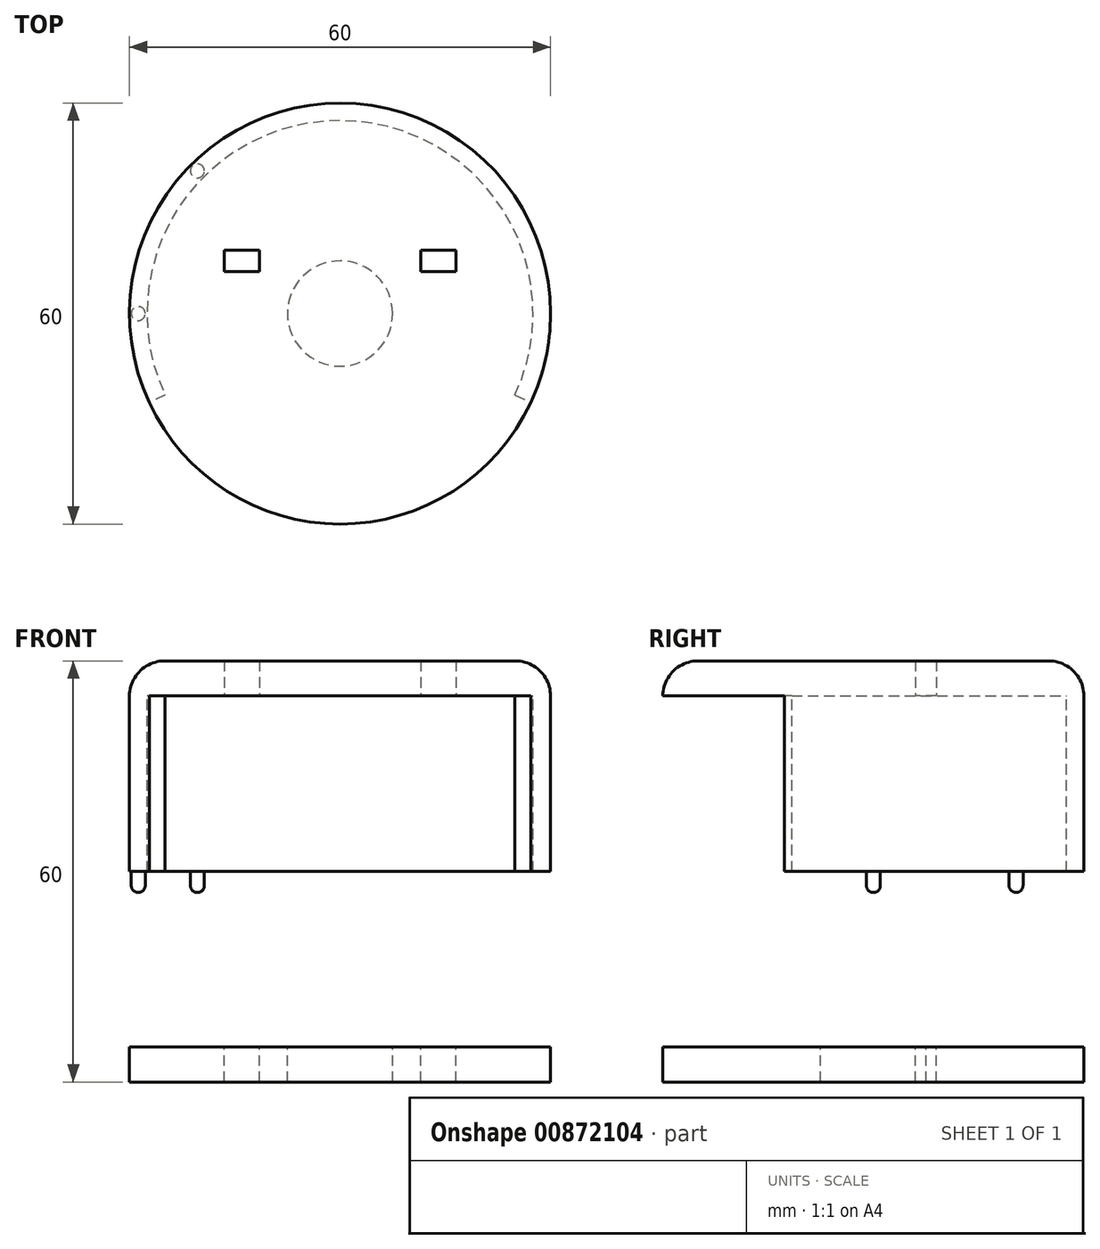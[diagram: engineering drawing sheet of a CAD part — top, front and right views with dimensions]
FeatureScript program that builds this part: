
annotation { "Feature Type Name" : "Feature", "Feature Type Description" : "" }
export const myFeature = defineFeature(function(context is Context, id is Id, definition is map)
    precondition{}
    {
        {
            var Q0;
            Q0=qCreatedBy(makeId("Top.planeOp"),FACE);
            var sketch = newSketch(context, id + "F0", { "sketchPlane" : qUnion([Q0])});
            skCircle(sketch, "E0", {"center": v(0, 0) * mm, "radius": 30 * mm});
            skLineSegment(sketch, "E1", {"start": v(0, 0) * mm, "end": v(0, 7.5) * mm});
            skLineSegment(sketch, "E2", {"start": v(0, 7.5) * mm, "end": v(14, 7.5) * mm});
            skLineSegment(sketch, "E3.bottom", {"start": v(11.5, 9) * mm, "end": v(16.5, 9) * mm});
            skLineSegment(sketch, "E3.top", {"start": v(11.5, 6) * mm, "end": v(16.5, 6) * mm});
            skLineSegment(sketch, "E3.left", {"start": v(11.5, 9) * mm, "end": v(11.5, 6) * mm});
            skLineSegment(sketch, "E3.right", {"start": v(16.5, 9) * mm, "end": v(16.5, 6) * mm});
            skPoint(sketch, "E3.middle", {"position": v(14, 7.5) * mm});
            skLineSegment(sketch, "E4", {"start": v(0, 7.5) * mm, "end": v(-14, 7.5) * mm});
            skLineSegment(sketch, "E5.bottom", {"start": v(-16.5, 9) * mm, "end": v(-11.5, 9) * mm});
            skLineSegment(sketch, "E5.top", {"start": v(-16.5, 6) * mm, "end": v(-11.5, 6) * mm});
            skLineSegment(sketch, "E5.left", {"start": v(-16.5, 9) * mm, "end": v(-16.5, 6) * mm});
            skLineSegment(sketch, "E5.right", {"start": v(-11.5, 9) * mm, "end": v(-11.5, 6) * mm});
            skPoint(sketch, "E5.middle", {"position": v(-14, 7.5) * mm});
            skLineSegment(sketch, "E6", {"start": v(0, 0) * mm, "end": v(-27.19, -12.68) * mm});
            skLineSegment(sketch, "E7", {"start": v(0, 0) * mm, "end": v(27.19, -12.68) * mm});
            skCircle(sketch, "E8", {"center": v(0, 0) * mm, "radius": 27.5 * mm});
            skCircle(sketch, "E9", {"center": v(0, 0) * mm, "radius": 7.5 * mm});
            skSolve(sketch);
        }
        {
            var Q0;
            Q0=makeQuery(id+"F0.imprint","IMPRINT",FACE,{"disambiguationData":[TD([[makeQuery(id+"F0.imprint","IMPRINT",EDGE,{"derivedFrom":sQuery(id+"F0.wireOp",EDGE,"E0")}),1.0]])]});
            var Q1;
            {var subQ4=sQuery(id+"F0.wireOp",EDGE,"E3.bottom");Q1=makeQuery(id+"F0.imprint","IMPRINT",FACE,{"disambiguationData":[TD([[makeQuery(id+"F0.imprint","IMPRINT",EDGE,{"derivedFrom":subQ4}),1.0]])]});}
            var Q2;
            {var subQ0=sQuery(id+"F0.wireOp",EDGE,"E9");var subQ1=sQuery(id+"F0.wireOp",EDGE,"E6");var subQ2=makeQuery(id+"F0.imprint","INTERSECT",VERTEX,{"derivedFrom":[subQ1,subQ0]});Q2=makeQuery(id+"F0.imprint","IMPRINT",FACE,{"disambiguationData":[TD([[makeQuery(id+"F0.imprint","IMPRINT",EDGE,{"disambiguationData":[TD([[subQ2,-1.0]])],"derivedFrom":subQ1}),1.0]])]});}
            extrude(context, id + "F1", {"entities" : qUnion([Q0, Q1, Q2]), "oppositeDirection" : true, "depth" : 5 * mm, "offsetDistance" : 25 * mm});
        }
        {
            var Q0;
            Q0=makeQuery(id+"F1.opExtrude","CAP_FACE",FACE,{"disambiguationData":[OSD([sQuery(id+"F0.wireOp",EDGE,"E0")])],"isStart":true});
            cPlane(context, id + "F2", {"entities" : qUnion([Q0]), "cplaneType" : CPlaneType.OFFSET, "offset" : 50 * mm, "width" : 150 * mm, "height" : 150 * mm});
        }
        {
            var Q0;
            Q0=qCreatedBy(id+"F2.planeOp",FACE);
            var sketch = newSketch(context, id + "F3", { "sketchPlane" : qUnion([Q0])});
            skCircle(sketch, "E10", {"center": v(0, 0) * mm, "radius": 30 * mm});
            skLineSegment(sketch, "E11", {"start": v(0, 0) * mm, "end": v(0, 7.5) * mm});
            skLineSegment(sketch, "E12", {"start": v(0, 7.5) * mm, "end": v(14, 7.5) * mm});
            skLineSegment(sketch, "E13", {"start": v(0, 7.5) * mm, "end": v(-14, 7.5) * mm});
            skLineSegment(sketch, "E14.bottom", {"start": v(-16.5, 9) * mm, "end": v(-11.5, 9) * mm});
            skLineSegment(sketch, "E14.top", {"start": v(-16.5, 6) * mm, "end": v(-11.5, 6) * mm});
            skLineSegment(sketch, "E14.left", {"start": v(-16.5, 9) * mm, "end": v(-16.5, 6) * mm});
            skLineSegment(sketch, "E14.right", {"start": v(-11.5, 9) * mm, "end": v(-11.5, 6) * mm});
            skPoint(sketch, "E14.middle", {"position": v(-14, 7.5) * mm});
            skLineSegment(sketch, "E15.bottom", {"start": v(16.5, 9) * mm, "end": v(11.5, 9) * mm});
            skLineSegment(sketch, "E15.top", {"start": v(16.5, 6) * mm, "end": v(11.5, 6) * mm});
            skLineSegment(sketch, "E15.left", {"start": v(16.5, 9) * mm, "end": v(16.5, 6) * mm});
            skLineSegment(sketch, "E15.right", {"start": v(11.5, 9) * mm, "end": v(11.5, 6) * mm});
            skPoint(sketch, "E15.middle", {"position": v(14, 7.5) * mm});
            skLineSegment(sketch, "E16", {"start": v(0, 0) * mm, "end": v(30, 0) * mm});
            skLineSegment(sketch, "E17", {"start": v(0, 0) * mm, "end": v(-30, 0) * mm});
            skCircle(sketch, "E18", {"center": v(0, 0) * mm, "radius": 27.5 * mm});
            skLineSegment(sketch, "E19", {"start": v(0, 0) * mm, "end": v(-27.19, -12.68) * mm});
            skLineSegment(sketch, "E20", {"start": v(0, 0) * mm, "end": v(27.19, -12.68) * mm});
            skLineSegment(sketch, "E21", {"start": v(0, 0) * mm, "end": v(-21.21, 21.21) * mm});
            skLineSegment(sketch, "E22", {"start": v(0, 0) * mm, "end": v(21.21, 21.21) * mm});
            skCircle(sketch, "E23", {"center": v(-28.75, 0) * mm, "radius": 1 * mm});
            skCircle(sketch, "E24", {"center": v(-20.33, 20.33) * mm, "radius": 1 * mm});
            skSolve(sketch);
        }
        {
            var Q0;
            {var subQ7=sQuery(id+"F3.wireOp",EDGE,"E14.bottom");Q0=makeQuery(id+"F3.imprint","IMPRINT",FACE,{"disambiguationData":[TD([[makeQuery(id+"F3.imprint","IMPRINT",EDGE,{"derivedFrom":subQ7}),1.0]])]});}
            var Q1;
            {var subQ1=sQuery(id+"F3.wireOp",EDGE,"E17");var subQ3=sQuery(id+"F3.wireOp",EDGE,"E18");var subQ4=makeQuery(id+"F3.imprint","INTERSECT",VERTEX,{"derivedFrom":[subQ1,subQ3]});Q1=makeQuery(id+"F3.imprint","IMPRINT",FACE,{"disambiguationData":[TD([[makeQuery(id+"F3.imprint","IMPRINT",EDGE,{"disambiguationData":[TD([[subQ4,-1.0]])],"derivedFrom":subQ3}),1.0]])]});}
            var Q2;
            {var subQ0=sQuery(id+"F3.wireOp",EDGE,"E19");var subQ1=sQuery(id+"F3.wireOp",EDGE,"E18");var subQ2=makeQuery(id+"F3.imprint","INTERSECT",VERTEX,{"derivedFrom":[subQ1,subQ0]});Q2=makeQuery(id+"F3.imprint","IMPRINT",FACE,{"disambiguationData":[TD([[makeQuery(id+"F3.imprint","IMPRINT",EDGE,{"disambiguationData":[TD([[subQ2,-1.0]])],"derivedFrom":subQ1}),1.0]])]});}
            var Q3;
            {var subQ1=sQuery(id+"F3.wireOp",EDGE,"E16");var subQ3=sQuery(id+"F3.wireOp",EDGE,"E18");var subQ4=makeQuery(id+"F3.imprint","INTERSECT",VERTEX,{"derivedFrom":[subQ1,subQ3]});Q3=makeQuery(id+"F3.imprint","IMPRINT",FACE,{"disambiguationData":[TD([[makeQuery(id+"F3.imprint","IMPRINT",EDGE,{"disambiguationData":[TD([[subQ4,1.0]])],"derivedFrom":subQ3}),1.0]])]});}
            var Q4;
            {var subQ0=sQuery(id+"F3.wireOp",EDGE,"E17");var subQ1=sQuery(id+"F3.wireOp",EDGE,"E10");var subQ2=makeQuery(id+"F3.imprint","INTERSECT",VERTEX,{"derivedFrom":[subQ1,subQ0]});Q4=makeQuery(id+"F3.imprint","IMPRINT",FACE,{"disambiguationData":[TD([[makeQuery(id+"F3.imprint","IMPRINT",EDGE,{"disambiguationData":[TD([[subQ2,-1.0]])],"derivedFrom":subQ1}),1.0]])]});}
            var Q5;
            {var subQ0=sQuery(id+"F3.wireOp",EDGE,"E19");var subQ1=sQuery(id+"F3.wireOp",EDGE,"E10");var subQ2=makeQuery(id+"F3.imprint","INTERSECT",VERTEX,{"derivedFrom":[subQ1,subQ0]});Q5=makeQuery(id+"F3.imprint","IMPRINT",FACE,{"disambiguationData":[TD([[makeQuery(id+"F3.imprint","IMPRINT",EDGE,{"disambiguationData":[TD([[subQ2,-1.0]])],"derivedFrom":subQ1}),1.0]])]});}
            var Q6;
            {var subQ0=sQuery(id+"F3.wireOp",EDGE,"E16");var subQ1=sQuery(id+"F3.wireOp",EDGE,"E10");var subQ2=makeQuery(id+"F3.imprint","INTERSECT",VERTEX,{"derivedFrom":[subQ1,subQ0]});Q6=makeQuery(id+"F3.imprint","IMPRINT",FACE,{"disambiguationData":[TD([[makeQuery(id+"F3.imprint","IMPRINT",EDGE,{"disambiguationData":[TD([[subQ2,1.0]])],"derivedFrom":subQ1}),1.0]])]});}
            var Q7;
            {var subQ0=sQuery(id+"F3.wireOp",EDGE,"E16");var subQ1=sQuery(id+"F3.wireOp",EDGE,"E10");var subQ2=makeQuery(id+"F3.imprint","INTERSECT",VERTEX,{"derivedFrom":[subQ1,subQ0]});Q7=makeQuery(id+"F3.imprint","IMPRINT",FACE,{"disambiguationData":[TD([[makeQuery(id+"F3.imprint","IMPRINT",EDGE,{"disambiguationData":[TD([[subQ2,-1.0]])],"derivedFrom":subQ1}),1.0]])]});}
            var Q8;
            {var subQ1=sQuery(id+"F3.wireOp",EDGE,"E15.bottom");Q8=makeQuery(id+"F3.imprint","IMPRINT",FACE,{"disambiguationData":[TD([[makeQuery(id+"F3.imprint","IMPRINT",EDGE,{"derivedFrom":subQ1}),-1.0]])]});}
            var Q9;
            {var subQ0=sQuery(id+"F3.wireOp",EDGE,"E23");var subQ1=sQuery(id+"F3.wireOp",EDGE,"E17");var subQ2=makeQuery(id+"F3.imprint","INTERSECT",VERTEX,{"disambiguationData":[OD(0.0)],"derivedFrom":[subQ1,subQ0]});Q9=makeQuery(id+"F3.imprint","IMPRINT",FACE,{"disambiguationData":[TD([[makeQuery(id+"F3.imprint","IMPRINT",EDGE,{"disambiguationData":[TD([[subQ2,-1.0]])],"derivedFrom":subQ1}),-1.0]])]});}
            var Q10;
            {var subQ0=sQuery(id+"F3.wireOp",EDGE,"E23");var subQ1=sQuery(id+"F3.wireOp",EDGE,"E17");var subQ2=makeQuery(id+"F3.imprint","INTERSECT",VERTEX,{"disambiguationData":[OD(0.0)],"derivedFrom":[subQ1,subQ0]});Q10=makeQuery(id+"F3.imprint","IMPRINT",FACE,{"disambiguationData":[TD([[makeQuery(id+"F3.imprint","IMPRINT",EDGE,{"disambiguationData":[TD([[subQ2,-1.0]])],"derivedFrom":subQ1}),1.0]])]});}
            var Q11;
            {var subQ0=sQuery(id+"F3.wireOp",EDGE,"E17");var subQ1=sQuery(id+"F3.wireOp",EDGE,"E10");var subQ2=makeQuery(id+"F3.imprint","INTERSECT",VERTEX,{"derivedFrom":[subQ1,subQ0]});Q11=makeQuery(id+"F3.imprint","IMPRINT",FACE,{"disambiguationData":[TD([[makeQuery(id+"F3.imprint","IMPRINT",EDGE,{"disambiguationData":[TD([[subQ2,1.0]])],"derivedFrom":subQ1}),1.0]])]});}
            var Q12;
            {var subQ0=sQuery(id+"F3.wireOp",EDGE,"E24");var subQ1=sQuery(id+"F3.wireOp",EDGE,"E21");var subQ2=makeQuery(id+"F3.imprint","INTERSECT",VERTEX,{"disambiguationData":[OD(0.0)],"derivedFrom":[subQ1,subQ0]});Q12=makeQuery(id+"F3.imprint","IMPRINT",FACE,{"disambiguationData":[TD([[makeQuery(id+"F3.imprint","IMPRINT",EDGE,{"disambiguationData":[TD([[subQ2,-1.0]])],"derivedFrom":subQ1}),1.0]])]});}
            var Q13;
            {var subQ0=sQuery(id+"F3.wireOp",EDGE,"E24");var subQ1=sQuery(id+"F3.wireOp",EDGE,"E21");var subQ2=makeQuery(id+"F3.imprint","INTERSECT",VERTEX,{"disambiguationData":[OD(0.0)],"derivedFrom":[subQ1,subQ0]});Q13=makeQuery(id+"F3.imprint","IMPRINT",FACE,{"disambiguationData":[TD([[makeQuery(id+"F3.imprint","IMPRINT",EDGE,{"disambiguationData":[TD([[subQ2,-1.0]])],"derivedFrom":subQ1}),-1.0]])]});}
            var Q14;
            {var subQ0=sQuery(id+"F3.wireOp",EDGE,"E21");var subQ1=sQuery(id+"F3.wireOp",EDGE,"E10");var subQ2=makeQuery(id+"F3.imprint","INTERSECT",VERTEX,{"derivedFrom":[subQ1,subQ0]});Q14=makeQuery(id+"F3.imprint","IMPRINT",FACE,{"disambiguationData":[TD([[makeQuery(id+"F3.imprint","IMPRINT",EDGE,{"disambiguationData":[TD([[subQ2,1.0]])],"derivedFrom":subQ1}),1.0]])]});}
            var Q15;
            {var subQ3=sQuery(id+"F3.wireOp",EDGE,"E18");var subQ5=sQuery(id+"F3.wireOp",EDGE,"E22");var subQ6=makeQuery(id+"F3.imprint","INTERSECT",VERTEX,{"derivedFrom":[subQ3,subQ5]});Q15=makeQuery(id+"F3.imprint","IMPRINT",FACE,{"disambiguationData":[TD([[makeQuery(id+"F3.imprint","IMPRINT",EDGE,{"disambiguationData":[TD([[subQ6,-1.0]])],"derivedFrom":subQ3}),1.0]])]});}
            var Q16;
            {var subQ0=sQuery(id+"F3.wireOp",EDGE,"E11");Q16=makeQuery(id+"F3.imprint","IMPRINT",FACE,{"disambiguationData":[TD([[makeQuery(id+"F3.imprint","IMPRINT",EDGE,{"derivedFrom":subQ0}),1.0]])]});}
            var Q17;
            {var subQ0=sQuery(id+"F3.wireOp",EDGE,"E11");Q17=makeQuery(id+"F3.imprint","IMPRINT",FACE,{"disambiguationData":[TD([[makeQuery(id+"F3.imprint","IMPRINT",EDGE,{"derivedFrom":subQ0}),-1.0]])]});}
            extrude(context, id + "F4", {"entities" : qUnion([Q0, Q1, Q2, Q3, Q4, Q5, Q6, Q7, Q8, Q9, Q10, Q11, Q12, Q13, Q14, Q15, Q16, Q17]), "depth" : 5 * mm, "offsetDistance" : 25 * mm});
        }
        {
            var Q0;
            Q0=makeQuery(id+"F4.opExtrude","CAP_EDGE",EDGE,{"disambiguationData":[OSD([sQuery(id+"F3.wireOp",EDGE,"E10")])],"isStart":false});
            fillet(context, id + "F5", {"entities" : qUnion([Q0]), "radius" : 5 * mm, "tangentPropagation" : true, "allowEdgeOverflow" : false});
        }
        {
            var Q0;
            {var subQ0=sQuery(id+"F3.wireOp",EDGE,"E17");var subQ1=sQuery(id+"F3.wireOp",EDGE,"E10");var subQ2=makeQuery(id+"F3.imprint","INTERSECT",VERTEX,{"derivedFrom":[subQ1,subQ0]});Q0=makeQuery(id+"F3.imprint","IMPRINT",FACE,{"disambiguationData":[TD([[makeQuery(id+"F3.imprint","IMPRINT",EDGE,{"disambiguationData":[TD([[subQ2,-1.0]])],"derivedFrom":subQ1}),1.0]])]});}
            var Q1;
            {var subQ0=sQuery(id+"F3.wireOp",EDGE,"E16");var subQ1=sQuery(id+"F3.wireOp",EDGE,"E10");var subQ2=makeQuery(id+"F3.imprint","INTERSECT",VERTEX,{"derivedFrom":[subQ1,subQ0]});Q1=makeQuery(id+"F3.imprint","IMPRINT",FACE,{"disambiguationData":[TD([[makeQuery(id+"F3.imprint","IMPRINT",EDGE,{"disambiguationData":[TD([[subQ2,-1.0]])],"derivedFrom":subQ1}),1.0]])]});}
            var Q2;
            {var subQ0=sQuery(id+"F3.wireOp",EDGE,"E16");var subQ1=sQuery(id+"F3.wireOp",EDGE,"E10");var subQ2=makeQuery(id+"F3.imprint","INTERSECT",VERTEX,{"derivedFrom":[subQ1,subQ0]});Q2=makeQuery(id+"F3.imprint","IMPRINT",FACE,{"disambiguationData":[TD([[makeQuery(id+"F3.imprint","IMPRINT",EDGE,{"disambiguationData":[TD([[subQ2,1.0]])],"derivedFrom":subQ1}),1.0]])]});}
            var Q3;
            {var subQ0=sQuery(id+"F3.wireOp",EDGE,"E17");var subQ1=sQuery(id+"F3.wireOp",EDGE,"E10");var subQ2=makeQuery(id+"F3.imprint","INTERSECT",VERTEX,{"derivedFrom":[subQ1,subQ0]});Q3=makeQuery(id+"F3.imprint","IMPRINT",FACE,{"disambiguationData":[TD([[makeQuery(id+"F3.imprint","IMPRINT",EDGE,{"disambiguationData":[TD([[subQ2,1.0]])],"derivedFrom":subQ1}),1.0]])]});}
            var Q4;
            {var subQ0=sQuery(id+"F3.wireOp",EDGE,"E21");var subQ1=sQuery(id+"F3.wireOp",EDGE,"E10");var subQ2=makeQuery(id+"F3.imprint","INTERSECT",VERTEX,{"derivedFrom":[subQ1,subQ0]});Q4=makeQuery(id+"F3.imprint","IMPRINT",FACE,{"disambiguationData":[TD([[makeQuery(id+"F3.imprint","IMPRINT",EDGE,{"disambiguationData":[TD([[subQ2,1.0]])],"derivedFrom":subQ1}),1.0]])]});}
            extrude(context, id + "F6", {"entities" : qUnion([Q0, Q1, Q2, Q3, Q4]), "operationType" : NewBodyOperationType.ADD, "oppositeDirection" : true, "depth" : 25 * mm, "offsetDistance" : 25 * mm});
        }
        {
            var Q0;
            {var subQ0=sQuery(id+"F3.wireOp",EDGE,"E23");var subQ1=sQuery(id+"F3.wireOp",EDGE,"E17");var subQ2=makeQuery(id+"F3.imprint","INTERSECT",VERTEX,{"disambiguationData":[OD(0.0)],"derivedFrom":[subQ1,subQ0]});Q0=makeQuery(id+"F3.imprint","IMPRINT",FACE,{"disambiguationData":[TD([[makeQuery(id+"F3.imprint","IMPRINT",EDGE,{"disambiguationData":[TD([[subQ2,-1.0]])],"derivedFrom":subQ1}),1.0]])]});}
            var Q1;
            {var subQ0=sQuery(id+"F3.wireOp",EDGE,"E23");var subQ1=sQuery(id+"F3.wireOp",EDGE,"E17");var subQ2=makeQuery(id+"F3.imprint","INTERSECT",VERTEX,{"disambiguationData":[OD(0.0)],"derivedFrom":[subQ1,subQ0]});Q1=makeQuery(id+"F3.imprint","IMPRINT",FACE,{"disambiguationData":[TD([[makeQuery(id+"F3.imprint","IMPRINT",EDGE,{"disambiguationData":[TD([[subQ2,-1.0]])],"derivedFrom":subQ1}),-1.0]])]});}
            var Q2;
            {var subQ0=sQuery(id+"F3.wireOp",EDGE,"E24");var subQ1=sQuery(id+"F3.wireOp",EDGE,"E21");var subQ2=makeQuery(id+"F3.imprint","INTERSECT",VERTEX,{"disambiguationData":[OD(0.0)],"derivedFrom":[subQ1,subQ0]});Q2=makeQuery(id+"F3.imprint","IMPRINT",FACE,{"disambiguationData":[TD([[makeQuery(id+"F3.imprint","IMPRINT",EDGE,{"disambiguationData":[TD([[subQ2,-1.0]])],"derivedFrom":subQ1}),1.0]])]});}
            var Q3;
            {var subQ0=sQuery(id+"F3.wireOp",EDGE,"E24");var subQ1=sQuery(id+"F3.wireOp",EDGE,"E21");var subQ2=makeQuery(id+"F3.imprint","INTERSECT",VERTEX,{"disambiguationData":[OD(0.0)],"derivedFrom":[subQ1,subQ0]});Q3=makeQuery(id+"F3.imprint","IMPRINT",FACE,{"disambiguationData":[TD([[makeQuery(id+"F3.imprint","IMPRINT",EDGE,{"disambiguationData":[TD([[subQ2,-1.0]])],"derivedFrom":subQ1}),-1.0]])]});}
            extrude(context, id + "F7", {"entities" : qUnion([Q0, Q1, Q2, Q3]), "operationType" : NewBodyOperationType.ADD, "oppositeDirection" : true, "depth" : 28 * mm, "offsetDistance" : 25 * mm});
        }
        {
            var Q0;
            Q0=makeQuery(id+"F7.opExtrude","CAP_EDGE",EDGE,{"disambiguationData":[OSD([sQuery(id+"F3.wireOp",EDGE,"E23")])],"isStart":false});
            var Q1;
            Q1=makeQuery(id+"F7.opExtrude","CAP_EDGE",EDGE,{"disambiguationData":[OSD([sQuery(id+"F3.wireOp",EDGE,"E24")])],"isStart":false});
            fillet(context, id + "F8", {"entities" : qUnion([Q0, Q1]), "radius" : 1 * mm, "tangentPropagation" : true, "allowEdgeOverflow" : false});
        }
    });
